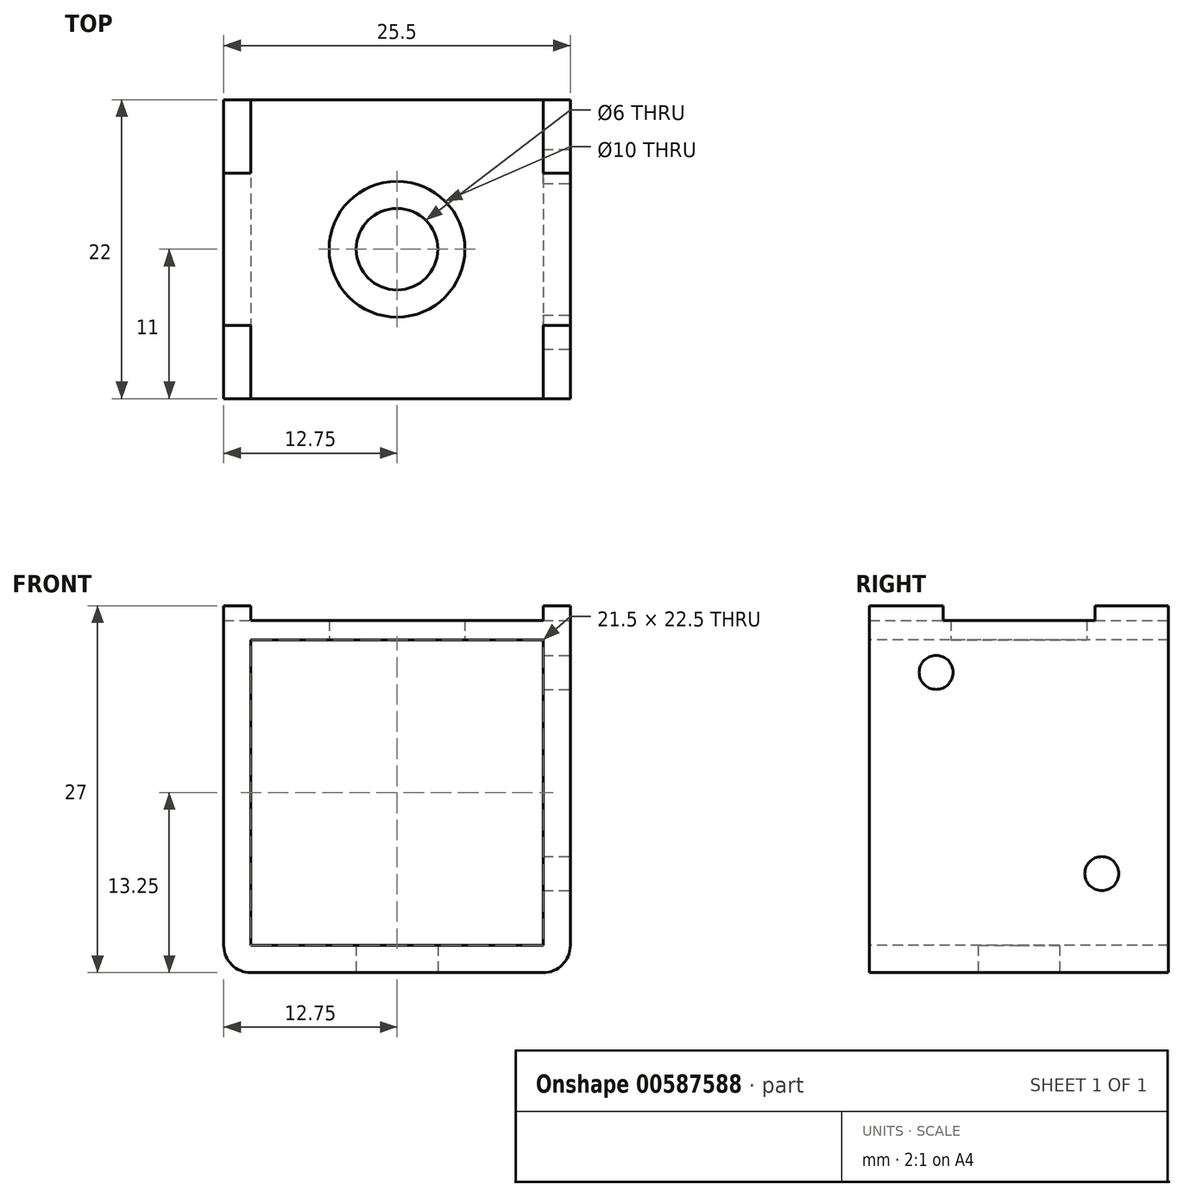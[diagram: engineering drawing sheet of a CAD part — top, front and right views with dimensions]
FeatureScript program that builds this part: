
annotation { "Feature Type Name" : "Feature", "Feature Type Description" : "" }
export const myFeature = defineFeature(function(context is Context, id is Id, definition is map)
    precondition{}
    {
        {
            var Q0;
            Q0=qCreatedBy(makeId("Top.planeOp"),FACE);
            var sketch = newSketch(context, id + "F0", { "sketchPlane" : qUnion([Q0])});
            skLineSegment(sketch, "E0.bottom", {"start": v(-12.75, 11) * mm, "end": v(12.75, 11) * mm});
            skLineSegment(sketch, "E0.top", {"start": v(-12.75, -11) * mm, "end": v(12.75, -11) * mm});
            skLineSegment(sketch, "E0.left", {"start": v(-12.75, 11) * mm, "end": v(-12.75, -11) * mm});
            skLineSegment(sketch, "E0.right", {"start": v(12.75, 11) * mm, "end": v(12.75, -11) * mm});
            skLineSegment(sketch, "E1", {"start": v(0, 0) * mm, "end": v(12.75, 11) * mm, "construction": true});
            skLineSegment(sketch, "E2", {"start": v(0, 0) * mm, "end": v(-12.75, -11) * mm, "construction": true});
            skLineSegment(sketch, "E3", {"start": v(-12.75, 11) * mm, "end": v(0, 0) * mm, "construction": true});
            skLineSegment(sketch, "E4", {"start": v(0, 0) * mm, "end": v(12.75, -11) * mm, "construction": true});
            skCircle(sketch, "E5", {"center": v(0, 0) * mm, "radius": 3 * mm});
            skSolve(sketch);
        }
        {
            var Q0;
            Q0 = qSketchRegion(id + "F0", true);
            extrude(context, id + "F1", {"entities" : qUnion([Q0]), "depth" : 2 * mm, "offsetDistance" : 25.4 * mm});
        }
        {
            var Q0;
            Q0=makeQuery(id+"F1.opExtrude","CAP_FACE",FACE,{"disambiguationData":[OSD([sQuery(id+"F0.wireOp",EDGE,"E0.bottom"),sQuery(id+"F0.wireOp",EDGE,"E0.top"),sQuery(id+"F0.wireOp",EDGE,"E0.left"),sQuery(id+"F0.wireOp",EDGE,"E0.right")])],"isStart":false});
            var sketch = newSketch(context, id + "F2", { "sketchPlane" : qUnion([Q0])});
            skLineSegment(sketch, "E6", {"start": v(-12.75, 11) * mm, "end": v(-10.75, 11) * mm});
            skLineSegment(sketch, "E7", {"start": v(-10.75, 11) * mm, "end": v(-10.75, -11) * mm});
            skLineSegment(sketch, "E8", {"start": v(-10.75, -11) * mm, "end": v(-12.75, -11) * mm});
            skLineSegment(sketch, "E9", {"start": v(12.75, 11) * mm, "end": v(10.75, 11) * mm});
            skLineSegment(sketch, "E10", {"start": v(10.75, 11) * mm, "end": v(10.75, -11) * mm});
            skLineSegment(sketch, "E11", {"start": v(10.75, -11) * mm, "end": v(12.75, -11) * mm});
            skLineSegment(sketch, "E12", {"start": v(-12.75, 5.6) * mm, "end": v(-10.75, 5.6) * mm});
            skLineSegment(sketch, "E13", {"start": v(-12.75, -5.6) * mm, "end": v(-10.75, -5.6) * mm});
            skLineSegment(sketch, "E14", {"start": v(10.75, 5.6) * mm, "end": v(12.75, 5.6) * mm});
            skLineSegment(sketch, "E15", {"start": v(10.75, -5.6) * mm, "end": v(12.75, -5.6) * mm});
            skSolve(sketch);
        }
        {
            var Q0;
            Q0 = qSketchRegion(id + "F2", true);
            var Q1;
            {var subQ0=sQuery(id+"F2.wireOp",EDGE,"E6");Q1=makeQuery(id+"F2.imprint","IMPRINT",FACE,{"disambiguationData":[TD([[makeQuery(id+"F2.imprint","IMPRINT",EDGE,{"derivedFrom":subQ0}),-1.0]])]});}
            var Q2;
            {var subQ0=sQuery(id+"F2.wireOp",EDGE,"E9");Q2=makeQuery(id+"F2.imprint","IMPRINT",FACE,{"disambiguationData":[TD([[makeQuery(id+"F2.imprint","IMPRINT",EDGE,{"derivedFrom":subQ0}),-1.0]])]});}
            var Q3;
            {var subQ0=sQuery(id+"F2.wireOp",EDGE,"E11");Q3=makeQuery(id+"F2.imprint","IMPRINT",FACE,{"disambiguationData":[TD([[makeQuery(id+"F2.imprint","IMPRINT",EDGE,{"derivedFrom":subQ0}),1.0]])]});}
            var Q4;
            {var subQ0=sQuery(id+"F2.wireOp",EDGE,"E8");Q4=makeQuery(id+"F2.imprint","IMPRINT",FACE,{"disambiguationData":[TD([[makeQuery(id+"F2.imprint","IMPRINT",EDGE,{"derivedFrom":subQ0}),1.0]])]});}
            extrude(context, id + "F3", {"entities" : qUnion([Q0, Q1, Q2, Q3, Q4]), "operationType" : NewBodyOperationType.ADD, "depth" : 25 * mm, "offsetDistance" : 25 * mm});
        }
        {
            var Q0;
            {var subQ0=sQuery(id+"F2.wireOp",EDGE,"E14");Q0=makeQuery(id+"F2.imprint","IMPRINT",FACE,{"disambiguationData":[TD([[makeQuery(id+"F2.imprint","IMPRINT",EDGE,{"derivedFrom":subQ0}),-1.0]])]});}
            var Q1;
            {var subQ0=sQuery(id+"F2.wireOp",EDGE,"E12");Q1=makeQuery(id+"F2.imprint","IMPRINT",FACE,{"disambiguationData":[TD([[makeQuery(id+"F2.imprint","IMPRINT",EDGE,{"derivedFrom":subQ0}),-1.0]])]});}
            extrude(context, id + "F4", {"entities" : qUnion([Q0, Q1]), "operationType" : NewBodyOperationType.ADD, "depth" : 22.5 * mm, "offsetDistance" : 25 * mm});
        }
        {
            var Q0;
            Q0=makeQuery(id+"F1.opExtrude","CAP_EDGE",EDGE,{"disambiguationData":[OSD([sQuery(id+"F0.wireOp",EDGE,"E0.right")])],"isStart":true});
            var Q1;
            Q1=makeQuery(id+"F1.opExtrude","CAP_EDGE",EDGE,{"disambiguationData":[OSD([sQuery(id+"F0.wireOp",EDGE,"E0.left")])],"isStart":true});
            fillet(context, id + "F5", {"entities" : qUnion([Q0, Q1]), "radius" : 2 * mm, "tangentPropagation" : true, "allowEdgeOverflow" : false});
        }
        {
            var Q0;
            Q0=makeQuery(id+"F4.opExtrude","CAP_FACE",FACE,{"disambiguationData":[OSD([sQuery(id+"F0.wireOp",EDGE,"E0.right"),sQuery(id+"F2.wireOp",EDGE,"E10"),sQuery(id+"F2.wireOp",EDGE,"E14"),sQuery(id+"F2.wireOp",EDGE,"E15")])],"isStart":false});
            var sketch = newSketch(context, id + "F6", { "sketchPlane" : qUnion([Q0])});
            skLineSegment(sketch, "E16", {"start": v(12.75, -5.6) * mm, "end": v(10.75, -5.6) * mm});
            skLineSegment(sketch, "E17", {"start": v(10.75, -5.6) * mm, "end": v(10.75, -11) * mm});
            skLineSegment(sketch, "E18", {"start": v(10.75, -11) * mm, "end": v(-10.75, -11) * mm});
            skLineSegment(sketch, "E19", {"start": v(-10.75, -11) * mm, "end": v(-10.75, -5.6) * mm});
            skLineSegment(sketch, "E20", {"start": v(-10.75, -5.6) * mm, "end": v(-12.75, -5.6) * mm});
            skLineSegment(sketch, "E21", {"start": v(-12.75, -5.6) * mm, "end": v(-12.75, 5.6) * mm});
            skLineSegment(sketch, "E22", {"start": v(-12.75, 5.6) * mm, "end": v(-10.75, 5.6) * mm});
            skLineSegment(sketch, "E23", {"start": v(-10.75, 5.6) * mm, "end": v(-10.75, 11) * mm});
            skLineSegment(sketch, "E24", {"start": v(-10.75, 11) * mm, "end": v(10.75, 11) * mm});
            skLineSegment(sketch, "E25", {"start": v(10.75, 11) * mm, "end": v(10.75, 5.6) * mm});
            skLineSegment(sketch, "E26", {"start": v(10.75, 5.6) * mm, "end": v(12.75, 5.6) * mm});
            skLineSegment(sketch, "E27", {"start": v(12.75, 5.6) * mm, "end": v(12.75, -5.6) * mm});
            skCircle(sketch, "E28", {"center": v(0, 0) * mm, "radius": 5 * mm});
            skSolve(sketch);
        }
        {
            var Q0;
            Q0 = qSketchRegion(id + "F6", true);
            extrude(context, id + "F7", {"entities" : qUnion([Q0]), "operationType" : NewBodyOperationType.ADD, "depth" : 1.42 * mm, "offsetDistance" : 25 * mm});
        }
        {
            var Q0;
            {var subQ0=sQuery(id+"F0.wireOp",EDGE,"E0.right");var subQ1=makeQuery(id+"F1.opExtrude","CAP_EDGE",EDGE,{"disambiguationData":[OSD([subQ0])],"isStart":false});Q0=makeQuery(id+"F7.boolean.opBoolean","MERGE",FACE,{"derivedFrom":[makeQuery(id+"F4.boolean.opBoolean","MERGE",FACE,{"derivedFrom":[makeQuery(id+"F3.boolean.opBoolean","MERGE",FACE,{"derivedFrom":[makeQuery(id+"F1.opExtrude","SWEPT_FACE",FACE,{"disambiguationData":[OSD([subQ0])]}),makeQuery(id+"F3.opExtrude","SWEPT_FACE",FACE,{"disambiguationData":[OSD([subQ0]),TDD([makeQuery(id+"F2.imprint","IMPRINT",EDGE,{"disambiguationData":[TD([[makeQuery(id+"F2.imprint","INTERSECT",VERTEX,{"derivedFrom":[subQ1,sQuery(id+"F2.wireOp",EDGE,"E9")]}),-1.0]])],"derivedFrom":subQ1})])]}),makeQuery(id+"F3.opExtrude","SWEPT_FACE",FACE,{"disambiguationData":[OSD([subQ0]),TDD([makeQuery(id+"F2.imprint","IMPRINT",EDGE,{"disambiguationData":[TD([[makeQuery(id+"F2.imprint","INTERSECT",VERTEX,{"derivedFrom":[subQ1,sQuery(id+"F2.wireOp",EDGE,"E11")]}),1.0]])],"derivedFrom":subQ1})])]})]}),makeQuery(id+"F4.opExtrude","SWEPT_FACE",FACE,{"disambiguationData":[OSD([subQ0])]})]}),makeQuery(id+"F7.opExtrude","SWEPT_FACE",FACE,{"disambiguationData":[OSD([sQuery(id+"F6.wireOp",EDGE,"E27")])]})]});}
            var sketch = newSketch(context, id + "F8", { "sketchPlane" : qUnion([Q0])});
            skCircle(sketch, "E29", {"center": v(-6.1, 22.1) * mm, "radius": 1.25 * mm});
            skCircle(sketch, "E30", {"center": v(6.1, 7.3) * mm, "radius": 1.25 * mm});
            skSolve(sketch);
        }
        {
            var Q0;
            Q0=makeQuery(id+"F8.imprint","IMPRINT",FACE,{"disambiguationData":[TD([[makeQuery(id+"F8.imprint","IMPRINT",EDGE,{"derivedFrom":sQuery(id+"F8.wireOp",EDGE,"E29")}),1.0]])]});
            var Q1;
            Q1=makeQuery(id+"F8.imprint","IMPRINT",FACE,{"disambiguationData":[TD([[makeQuery(id+"F8.imprint","IMPRINT",EDGE,{"derivedFrom":sQuery(id+"F8.wireOp",EDGE,"E30")}),1.0]])]});
            var Q2;
            {var subQ0=sQuery(id+"F0.wireOp",EDGE,"E0.top");var subQ1=sQuery(id+"F0.wireOp",EDGE,"E0.bottom");var subQ6=sQuery(id+"F2.wireOp",EDGE,"E10");Q2=makeQuery(id+"F7.boolean.opBoolean","SPLIT",FACE,{"disambiguationData":[TD([makeQuery(id+"F1.opExtrude","CAP_FACE",FACE,{"disambiguationData":[OSD([subQ1,subQ0,sQuery(id+"F0.wireOp",EDGE,"E0.left"),sQuery(id+"F0.wireOp",EDGE,"E0.right"),sQuery(id+"F0.wireOp",EDGE,"E5")])],"isStart":false})])],"derivedFrom":makeQuery(id+"F4.boolean.opBoolean","MERGE",FACE,{"derivedFrom":[makeQuery(id+"F3.opExtrude","SWEPT_FACE",FACE,{"disambiguationData":[OSD([subQ6]),TDD([makeQuery(id+"F2.imprint","IMPRINT",EDGE,{"disambiguationData":[TD([[makeQuery(id+"F2.imprint","INTERSECT",VERTEX,{"derivedFrom":[subQ6,sQuery(id+"F2.wireOp",EDGE,"E14")]}),1.0]])],"derivedFrom":subQ6})])]}),makeQuery(id+"F3.opExtrude","SWEPT_FACE",FACE,{"disambiguationData":[OSD([subQ6]),TDD([makeQuery(id+"F2.imprint","IMPRINT",EDGE,{"disambiguationData":[TD([[makeQuery(id+"F2.imprint","INTERSECT",VERTEX,{"derivedFrom":[subQ6,sQuery(id+"F2.wireOp",EDGE,"E15")]}),-1.0]])],"derivedFrom":subQ6})])]}),makeQuery(id+"F4.opExtrude","SWEPT_FACE",FACE,{"disambiguationData":[OSD([subQ6])]})]})});}
            extrude(context, id + "F9", {"entities" : qUnion([Q0, Q1]), "operationType" : NewBodyOperationType.REMOVE, "endBound" : BoundingType.UP_TO_SURFACE, "oppositeDirection" : true, "depth" : 25 * mm, "endBoundEntityFace" : qUnion([Q2]), "offsetDistance" : 25 * mm});
        }
    });
